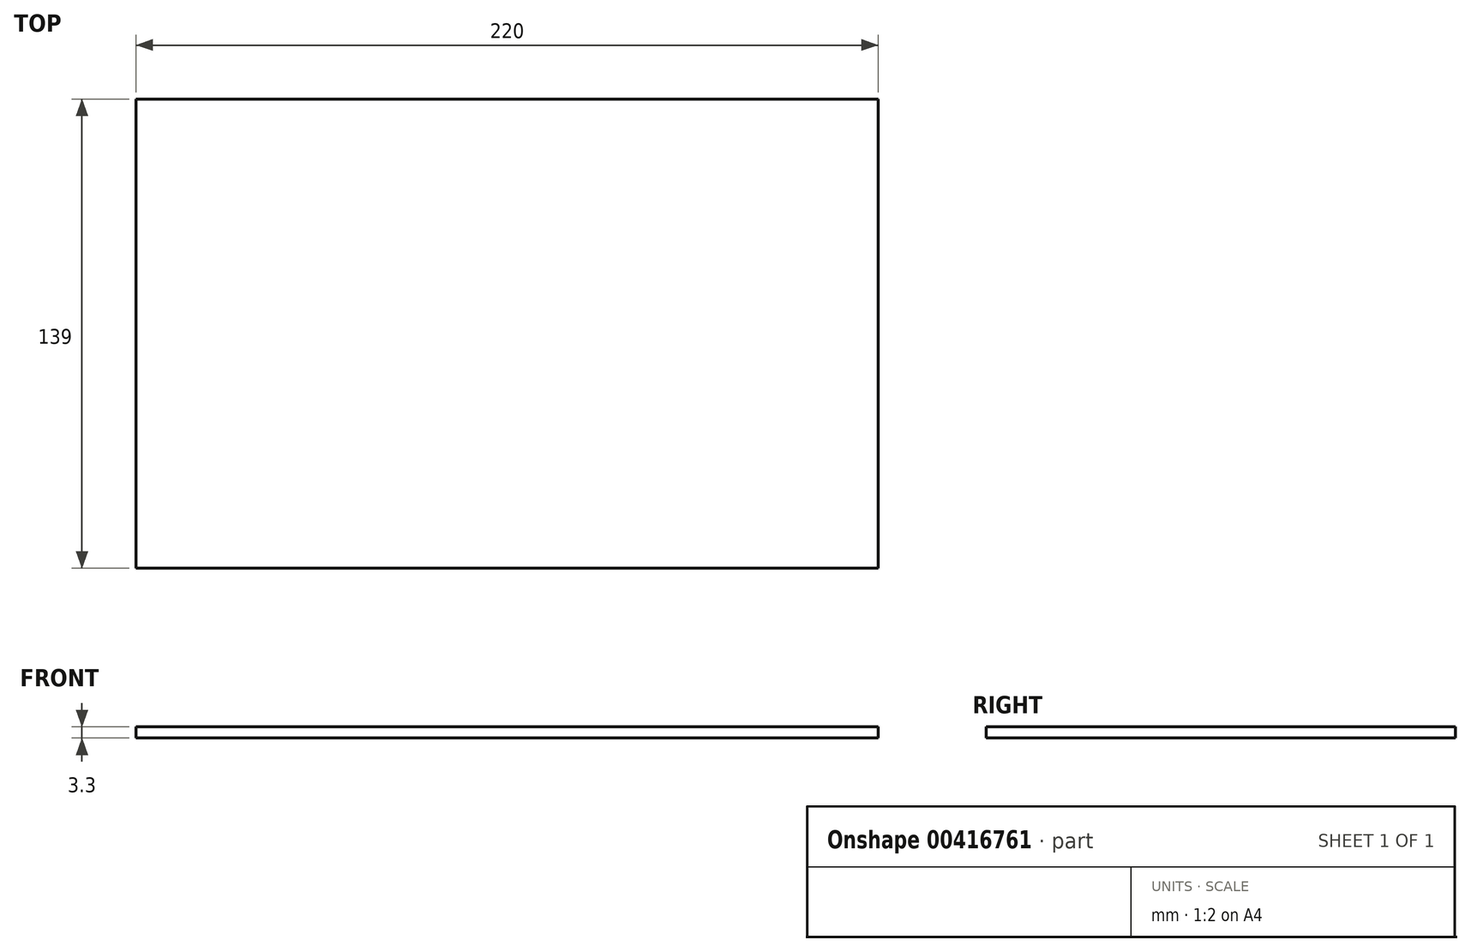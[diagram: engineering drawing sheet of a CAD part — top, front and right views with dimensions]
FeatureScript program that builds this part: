
annotation { "Feature Type Name" : "Feature", "Feature Type Description" : "" }
export const myFeature = defineFeature(function(context is Context, id is Id, definition is map)
    precondition{}
    {
        {
            var Q0;
            Q0=qCreatedBy(makeId("Top.planeOp"),FACE);
            var sketch = newSketch(context, id + "F0", { "sketchPlane" : qUnion([Q0])});
            skLineSegment(sketch, "E0.bottom", {"start": v(0, 0) * mm, "end": v(220, 0) * mm});
            skLineSegment(sketch, "E0.top", {"start": v(0, -139) * mm, "end": v(220, -139) * mm});
            skLineSegment(sketch, "E0.left", {"start": v(0, 0) * mm, "end": v(0, -139) * mm});
            skLineSegment(sketch, "E0.right", {"start": v(220, 0) * mm, "end": v(220, -139) * mm});
            skSolve(sketch);
        }
        {
            var Q0;
            Q0 = qSketchRegion(id + "F0", true);
            extrude(context, id + "F1", {"entities" : qUnion([Q0]), "depth" : 3.3 * mm});
        }
    });
